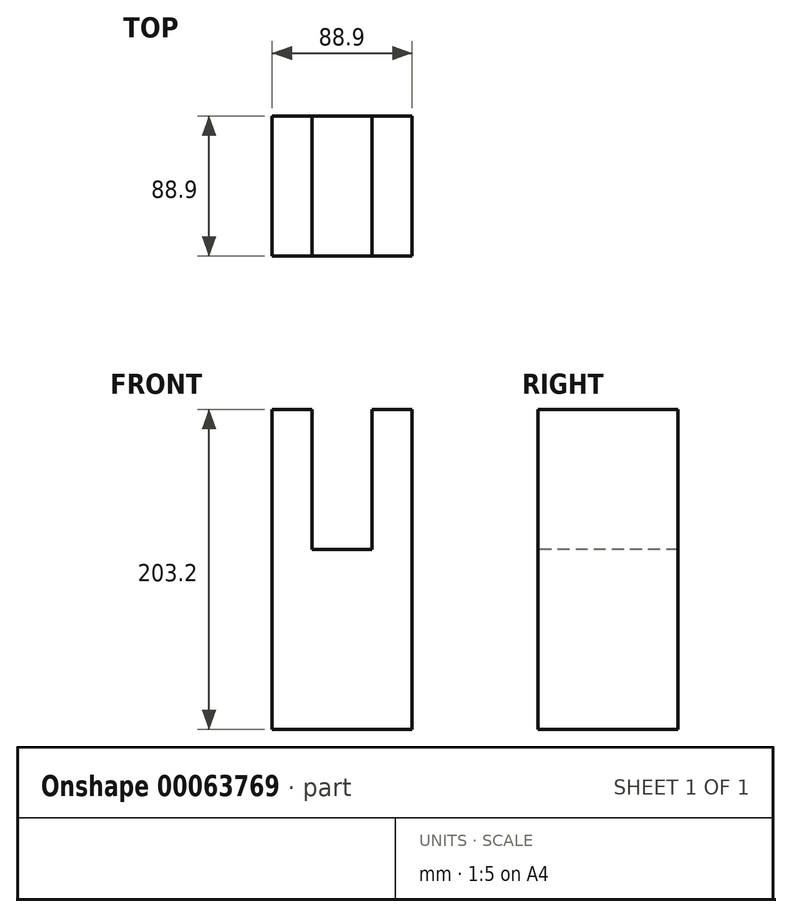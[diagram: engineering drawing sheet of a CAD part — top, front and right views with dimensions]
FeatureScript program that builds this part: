
annotation { "Feature Type Name" : "Feature", "Feature Type Description" : "" }
export const myFeature = defineFeature(function(context is Context, id is Id, definition is map)
    precondition{}
    {
        {
            var Q0;
            Q0=qCreatedBy(makeId("Top.planeOp"),FACE);
            var sketch = newSketch(context, id + "F0", { "sketchPlane" : qUnion([Q0])});
            skLineSegment(sketch, "E0.bottom", {"start": v(-41.76, 43.96) * mm, "end": v(47.14, 43.96) * mm});
            skLineSegment(sketch, "E0.top", {"start": v(-41.76, -44.94) * mm, "end": v(47.14, -44.94) * mm});
            skLineSegment(sketch, "E0.left", {"start": v(-41.76, 43.96) * mm, "end": v(-41.76, -44.94) * mm});
            skLineSegment(sketch, "E0.right", {"start": v(47.14, 43.96) * mm, "end": v(47.14, -44.94) * mm});
            skSolve(sketch);
        }
        {
            var Q0;
            Q0=qSketchRegion(id+"F0",true);
            extrude(context, id + "F1", {"entities" : qUnion([Q0]), "depth" : 203.2 * mm});
        }
        {
            var Q0;
            Q0=makeQuery(id+"F1.opExtrude","CAP_FACE",FACE,{"disambiguationData":[OSD([sQuery(id+"F0.wireOp",EDGE,"E0.bottom"),sQuery(id+"F0.wireOp",EDGE,"E0.top"),sQuery(id+"F0.wireOp",EDGE,"E0.left"),sQuery(id+"F0.wireOp",EDGE,"E0.right")])],"isStart":false});
            var sketch = newSketch(context, id + "F2", { "sketchPlane" : qUnion([Q0])});
            skLineSegment(sketch, "E1.bottom", {"start": v(-16.36, 43.96) * mm, "end": v(21.74, 43.96) * mm});
            skLineSegment(sketch, "E1.top", {"start": v(-16.36, -44.94) * mm, "end": v(21.74, -44.94) * mm});
            skLineSegment(sketch, "E1.left", {"start": v(-16.36, 43.96) * mm, "end": v(-16.36, -44.94) * mm});
            skLineSegment(sketch, "E1.right", {"start": v(21.74, 43.96) * mm, "end": v(21.74, -44.94) * mm});
            skSolve(sketch);
        }
        {
            var Q0;
            Q0=qSketchRegion(id+"F2",true);
            extrude(context, id + "F3", {"entities" : qUnion([Q0]), "operationType" : NewBodyOperationType.REMOVE, "oppositeDirection" : true, "depth" : 88.9 * mm});
        }
    });
